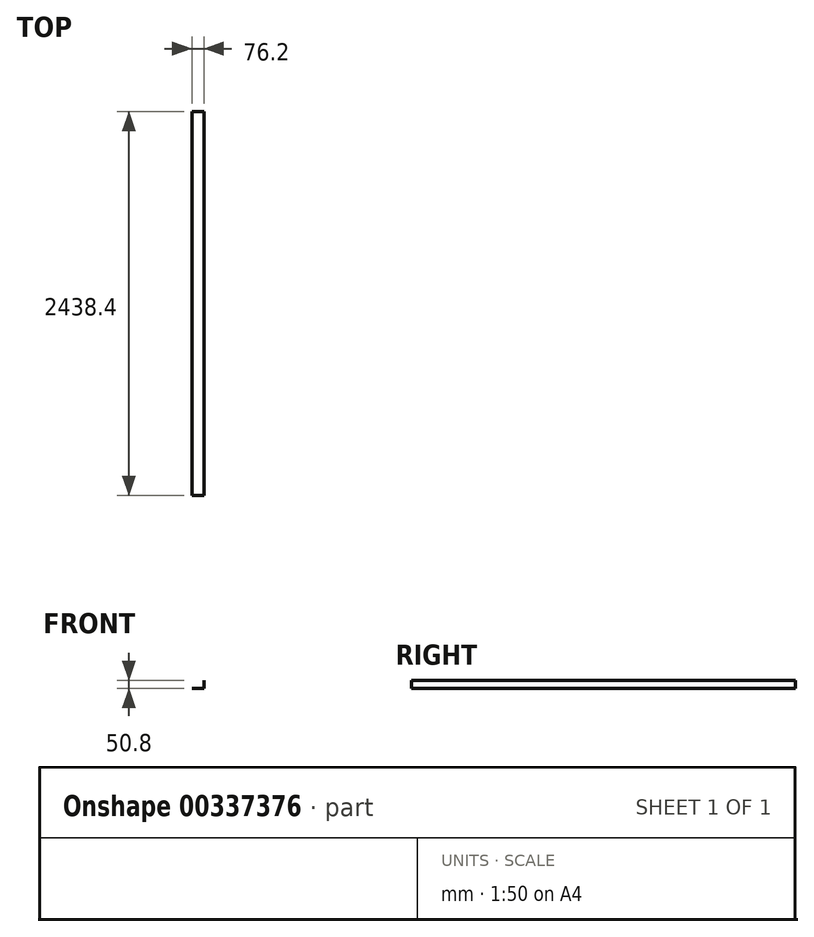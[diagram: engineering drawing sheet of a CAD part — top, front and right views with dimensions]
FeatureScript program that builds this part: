
annotation { "Feature Type Name" : "Feature", "Feature Type Description" : "" }
export const myFeature = defineFeature(function(context is Context, id is Id, definition is map)
    precondition{}
    {
        {
            var Q0;
            Q0=qCreatedBy(makeId("Front.planeOp"),FACE);
            var sketch = newSketch(context, id + "F0", { "sketchPlane" : qUnion([Q0])});
            skLineSegment(sketch, "E0", {"start": v(-408.92, 447.16) * mm, "end": v(-408.92, 396.36) * mm});
            skLineSegment(sketch, "E1", {"start": v(-408.92, 396.36) * mm, "end": v(-485.12, 396.36) * mm});
            skSolve(sketch);
        }
        {
            var Q0;
            Q0 = qSketchRegion(id + "F0", true);
            var Q1;
            Q1=sQuery(id+"F0.wireOp",EDGE,"E0");
            var Q2;
            Q2=sQuery(id+"F0.wireOp",EDGE,"E1");
            extrude(context, id + "F1", {"entities" : qUnion([Q0]), "bodyType" : ToolBodyType.SURFACE, "surfaceEntities" : qUnion([Q1, Q2]), "depth" : 2438.4 * mm});
        }
    });
